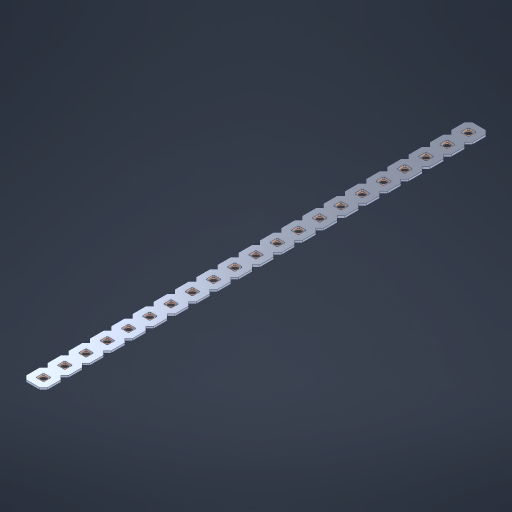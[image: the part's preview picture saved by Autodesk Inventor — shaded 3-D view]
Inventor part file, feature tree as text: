
AUTODESK INVENTOR PART (.ipt)
format: ipt  version: 2023 (Build 270158000, 158)  size: 528,896 bytes
history: native  units: in
note: dims shown in document units (in); Inventor stores cm internally (conversion verified against a paired STEP export)
features: other x22, extrude x20, sketch x2, pattern_linear x1
ambient origin geometry x8: Origin, YZ Plane, XZ Plane, XY Plane, X Axis, Y Axis, Z Axis, Center Point
bodies: Solid1 (feature_tree), Body (feature_tree)
feature tree (45):
  pattern_linear  "Rectangular Pattern1"  Spacing1=0.09in  [1 undecoded]
  sketch  "Sketch1"  dims[d1=0.5in]
  sketch  "Sketch2"  dims[d2=0.182in d3=0.09in d4=0.09in d5=0.09in d6=0.09in d7=0.09in d8=0.09in d9=0.09in d10=0.09in d11=0.02in d13=0.0in d14=0.172in d15=0.0625in d16=0.0in d19=0.5in d22=0.5in]
  other  "Srf1"
  other  "Srf126"
  other  "Srf127"
  other  "Srf128"
  other  "Srf129"
  other  "Srf130"
  other  "Srf131"
  other  "Srf250"
  other  "Srf251"
  other  "Srf252"
  other  "Srf253"
  other  "Srf254"
  other  "Srf255"
  other  "Srf256"
  other  "Srf257"
  other  "Srf258"
  other  "Srf259"
  other  "Srf260"
  other  "Srf261"
  other  "Srf262"
  other  "Srf263"
  other  "Circle"
  extrude  "ExtrusionSrf126"  Depth=0.09in
  extrude  "ExtrusionSrf127"  Depth=0.09in
  extrude  "ExtrusionSrf128"  Depth=0.09in
  extrude  "ExtrusionSrf129"  Depth=0.09in
  extrude  "ExtrusionSrf130"  Depth=0.09in
  extrude  "ExtrusionSrf131"  Depth=0.09in
  extrude  "ExtrusionSrf250"  Depth=0.09in
  extrude  "ExtrusionSrf251"  Depth=0.02in
  extrude  "ExtrusionSrf252"  TaperAngle=0.0deg  [1 undecoded]
  extrude  "ExtrusionSrf253"  Depth=0.5in
  extrude  "ExtrusionSrf254"  Depth=0.5in TaperAngle=0.0deg
  extrude  "ExtrusionSrf255"  Depth=0.5in
  extrude  "ExtrusionSrf256"  Depth=0.5in
  extrude  "ExtrusionSrf257"  [1 undecoded]
  extrude  "ExtrusionSrf258"  [1 undecoded]
  extrude  "ExtrusionSrf259"  [1 undecoded]
  extrude  "ExtrusionSrf260"  [1 undecoded]
  extrude  "ExtrusionSrf261"  [1 undecoded]
  extrude  "ExtrusionSrf262"  [1 undecoded]
  extrude  "ExtrusionSrf263"  [1 undecoded]
note: 9 required parameter values undecoded (feature->parameter linkage not recoverable at this tier; creation-order binding heuristic only, values carry confidence <= 0.55)
